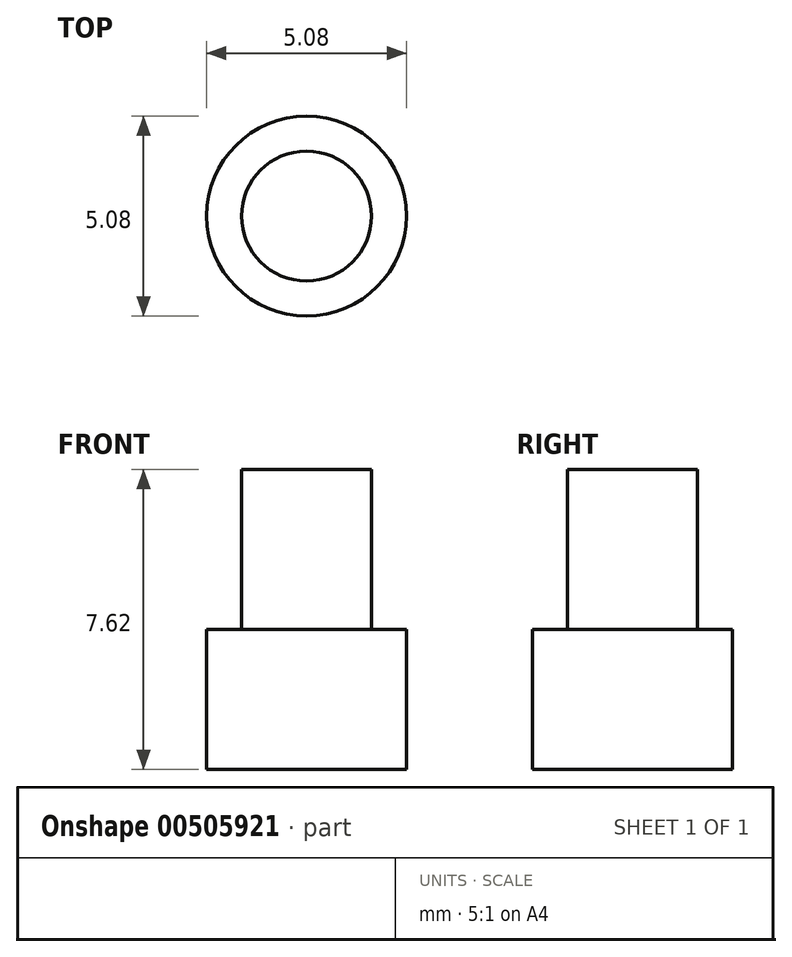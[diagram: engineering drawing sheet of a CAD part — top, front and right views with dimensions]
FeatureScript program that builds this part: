
annotation { "Feature Type Name" : "Feature", "Feature Type Description" : "" }
export const myFeature = defineFeature(function(context is Context, id is Id, definition is map)
    precondition{}
    {
        {
            var Q0;
            Q0=qCreatedBy(makeId("Top.planeOp"),FACE);
            var sketch = newSketch(context, id + "F0", { "sketchPlane" : qUnion([Q0])});
            skCircle(sketch, "E0", {"center": v(0, 0) * mm, "radius": 2.54 * mm});
            skSolve(sketch);
        }
        {
            var Q0;
            Q0=qSketchRegion(id+"F0",true);
            var Q1;
            Q1=makeQuery(id+"F0.imprint","IMPRINT",FACE,{"disambiguationData":[TD([[makeQuery(id+"F0.imprint","IMPRINT",EDGE,{"derivedFrom":sQuery(id+"F0.wireOp",EDGE,"E0")}),1.0]])]});
            extrude(context, id + "F1", {"entities" : qUnion([Q0, Q1]), "depth" : 3.56 * mm, "offsetDistance" : 25.4 * mm});
        }
        {
            var Q0;
            Q0=makeQuery(id+"F1.opExtrude","CAP_FACE",FACE,{"disambiguationData":[OSD([sQuery(id+"F0.wireOp",EDGE,"E0")])],"isStart":false});
            var sketch = newSketch(context, id + "F2", { "sketchPlane" : qUnion([Q0])});
            skCircle(sketch, "E1", {"center": v(0, 0) * mm, "radius": 1.65 * mm});
            skSolve(sketch);
        }
        {
            var Q0;
            Q0=makeQuery(id+"F2.imprint","IMPRINT",FACE,{"disambiguationData":[TD([[makeQuery(id+"F2.imprint","IMPRINT",EDGE,{"derivedFrom":sQuery(id+"F2.wireOp",EDGE,"E1")}),1.0]])]});
            extrude(context, id + "F3", {"entities" : qUnion([Q0]), "operationType" : NewBodyOperationType.ADD, "depth" : 4.06 * mm, "offsetDistance" : 25.4 * mm});
        }
    });
